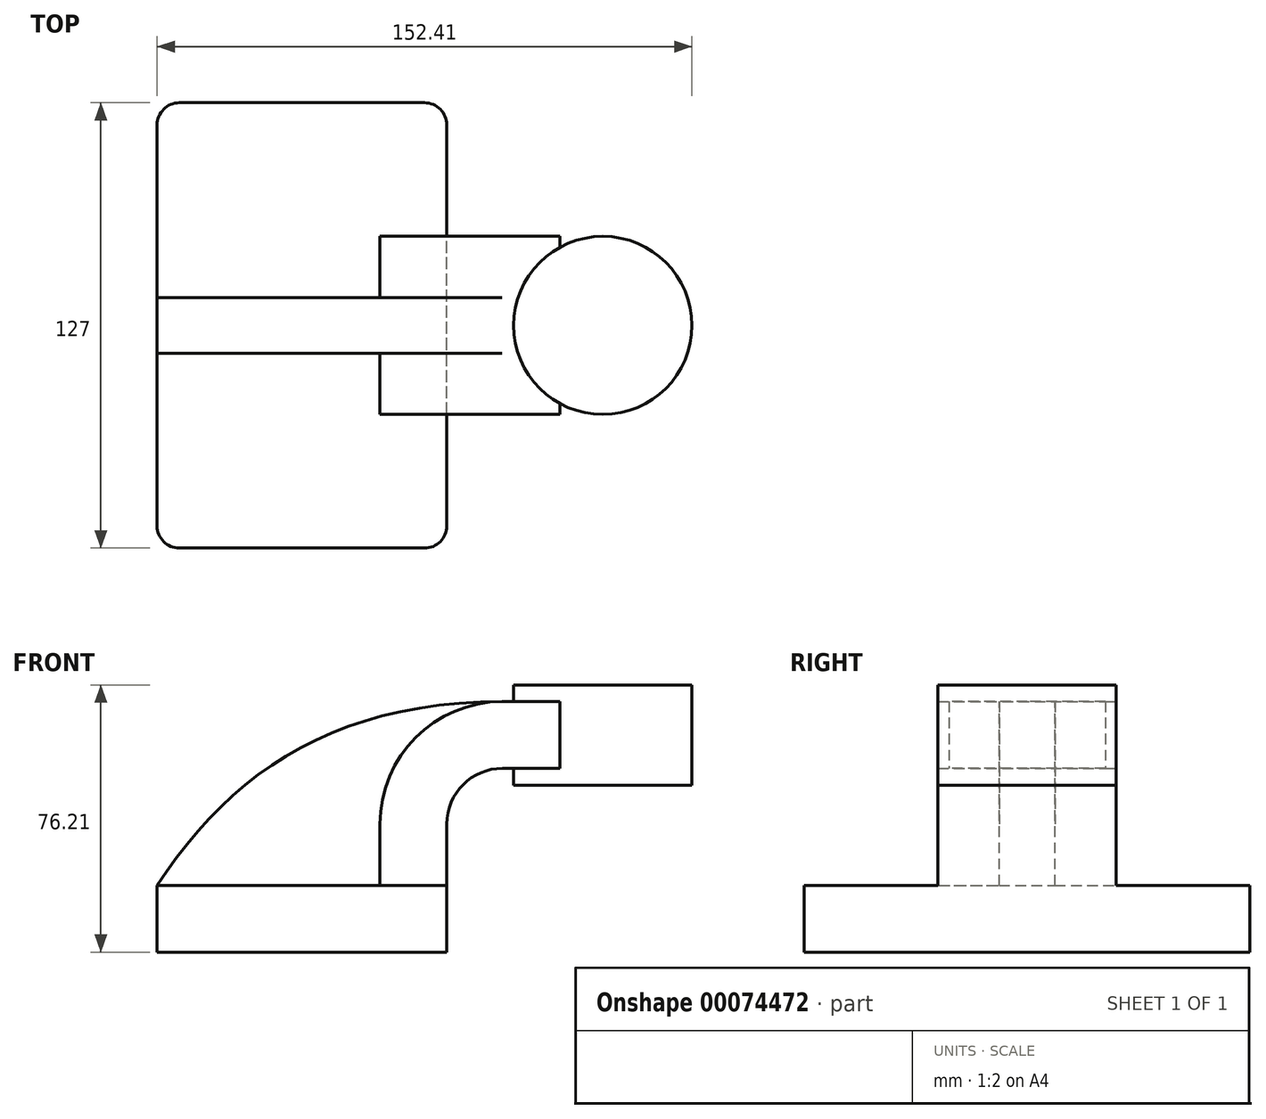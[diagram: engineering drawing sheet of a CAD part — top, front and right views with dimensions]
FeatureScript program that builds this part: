
annotation { "Feature Type Name" : "Feature", "Feature Type Description" : "" }
export const myFeature = defineFeature(function(context is Context, id is Id, definition is map)
    precondition{}
    {
        {
            var Q0;
            Q0=qCreatedBy(makeId("Front.planeOp"),FACE);
            var sketch = newSketch(context, id + "F0", { "sketchPlane" : qUnion([Q0])});
            skLineSegment(sketch, "E0.rect.bottom", {"start": v(-41.28, -9.53) * mm, "end": v(41.28, -9.53) * mm});
            skLineSegment(sketch, "E0.rect.top", {"start": v(-41.28, 9.53) * mm, "end": v(41.28, 9.53) * mm});
            skLineSegment(sketch, "E0.rect.left", {"start": v(-41.28, -9.53) * mm, "end": v(-41.28, 9.53) * mm});
            skLineSegment(sketch, "E0.rect.right", {"start": v(41.28, -9.53) * mm, "end": v(41.28, 9.53) * mm});
            skPoint(sketch, "E0.rect.middle", {"position": v(0, 0) * mm});
            skLineSegment(sketch, "E1.rect.bottom", {"start": v(60.32, 38.1) * mm, "end": v(111.12, 38.1) * mm});
            skLineSegment(sketch, "E1.rect.top", {"start": v(60.32, 66.67) * mm, "end": v(111.12, 66.67) * mm});
            skLineSegment(sketch, "E1.rect.left", {"start": v(60.32, 38.1) * mm, "end": v(60.32, 66.67) * mm});
            skLineSegment(sketch, "E1.rect.right", {"start": v(111.12, 38.1) * mm, "end": v(111.12, 66.67) * mm});
            skPoint(sketch, "E1.rect.middle", {"position": v(85.72, 52.39) * mm});
            skLineSegment(sketch, "E2", {"start": v(41.28, 9.53) * mm, "end": v(41.28, 27) * mm});
            skArc(sketch, "E3", {"start": v(41.27, 27) * mm, "mid": v(45.92, 38.23) * mm, "end": v(57.15, 42.88) * mm});
            skLineSegment(sketch, "E4", {"start": v(57.15, 42.88) * mm, "end": v(73.48, 42.88) * mm});
            skLineSegment(sketch, "E5.0", {"start": v(57.15, 61.93) * mm, "end": v(73.48, 61.93) * mm});
            skArc(sketch, "E5.1", {"start": v(22.22, 27) * mm, "mid": v(32.45, 51.7) * mm, "end": v(57.15, 61.93) * mm});
            skLineSegment(sketch, "E5.2", {"start": v(22.22, 9.53) * mm, "end": v(22.22, 27) * mm});
            skLineSegment(sketch, "E6", {"start": v(73.48, 42.88) * mm, "end": v(73.48, 61.93) * mm});
            skFitSpline(sketch, "E7", {"points": [v(-41.28, 9.52) * mm, v(57.15, 61.93) * mm], "startDerivative": vector(62.14, 95.05) * mm, "endDerivative": vector(145.48, 0.19) * mm});
            skLineSegment(sketch, "E8", {"start": v(85.72, 38.1) * mm, "end": v(85.72, 66.67) * mm});
            skSolve(sketch);
        }
        {
            var Q0;
            Q0=makeQuery(id+"F0.imprint","IMPRINT",FACE,{"disambiguationData":[TD([[makeQuery(id+"F0.imprint","IMPRINT",EDGE,{"derivedFrom":sQuery(id+"F0.wireOp",EDGE,"E0.rect.bottom")}),1.0]])]});
            extrude(context, id + "F1", {"entities" : qUnion([Q0]), "endBound" : BoundingType.SYMMETRIC, "depth" : 127 * mm});
        }
        {
            var Q0;
            {var subQ1=sQuery(id+"F0.wireOp",EDGE,"E2");Q0=makeQuery(id+"F0.imprint","IMPRINT",FACE,{"disambiguationData":[TD([[makeQuery(id+"F0.imprint","IMPRINT",EDGE,{"derivedFrom":subQ1}),1.0]])]});}
            var Q1;
            {var subQ5=sQuery(id+"F0.wireOp",EDGE,"E6");Q1=makeQuery(id+"F0.imprint","IMPRINT",FACE,{"disambiguationData":[TD([[makeQuery(id+"F0.imprint","IMPRINT",EDGE,{"derivedFrom":subQ5}),1.0]])]});}
            extrude(context, id + "F2", {"entities" : qUnion([Q0, Q1]), "operationType" : NewBodyOperationType.ADD, "endBound" : BoundingType.SYMMETRIC, "depth" : 50.8 * mm});
        }
        {
            var Q0;
            {var subQ3=sQuery(id+"F0.wireOp",EDGE,"E5.2");Q0=makeQuery(id+"F0.imprint","IMPRINT",FACE,{"disambiguationData":[TD([[makeQuery(id+"F0.imprint","IMPRINT",EDGE,{"derivedFrom":subQ3}),1.0]])]});}
            extrude(context, id + "F3", {"entities" : qUnion([Q0]), "operationType" : NewBodyOperationType.ADD, "endBound" : BoundingType.SYMMETRIC, "depth" : 15.88 * mm});
        }
        {
            var Q0;
            {var subQ0=sQuery(id+"F0.wireOp",EDGE,"E1.rect.right");Q0=makeQuery(id+"F0.imprint","IMPRINT",FACE,{"disambiguationData":[TD([[makeQuery(id+"F0.imprint","IMPRINT",EDGE,{"derivedFrom":subQ0}),1.0]])]});}
            var Q1;
            Q1=sQuery(id+"F0.wireOp",EDGE,"E8");
            revolve(context, id + "F4", {"operationType" : NewBodyOperationType.ADD, "entities" : qUnion([Q0]), "axis" : qUnion([Q1]), "revolveType" : RevolveType.FULL});
        }
        {
            var Q0;
            Q0=makeQuery(id+"F1.opExtrude","CAP_EDGE",EDGE,{"disambiguationData":[OSD([sQuery(id+"F0.wireOp",EDGE,"E0.rect.right")])],"isStart":false});
            var Q1;
            Q1=makeQuery(id+"F1.opExtrude","CAP_EDGE",EDGE,{"disambiguationData":[OSD([sQuery(id+"F0.wireOp",EDGE,"E0.rect.left")])],"isStart":false});
            var Q2;
            Q2=makeQuery(id+"F1.opExtrude","CAP_EDGE",EDGE,{"disambiguationData":[OSD([sQuery(id+"F0.wireOp",EDGE,"E0.rect.left")])],"isStart":true});
            var Q3;
            Q3=makeQuery(id+"F1.opExtrude","CAP_EDGE",EDGE,{"disambiguationData":[OSD([sQuery(id+"F0.wireOp",EDGE,"E0.rect.right")])],"isStart":true});
            fillet(context, id + "F5", {"entities" : qUnion([Q0, Q1, Q2, Q3]), "radius" : 6.35 * mm, "tangentPropagation" : true, "allowEdgeOverflow" : false});
        }
    });
